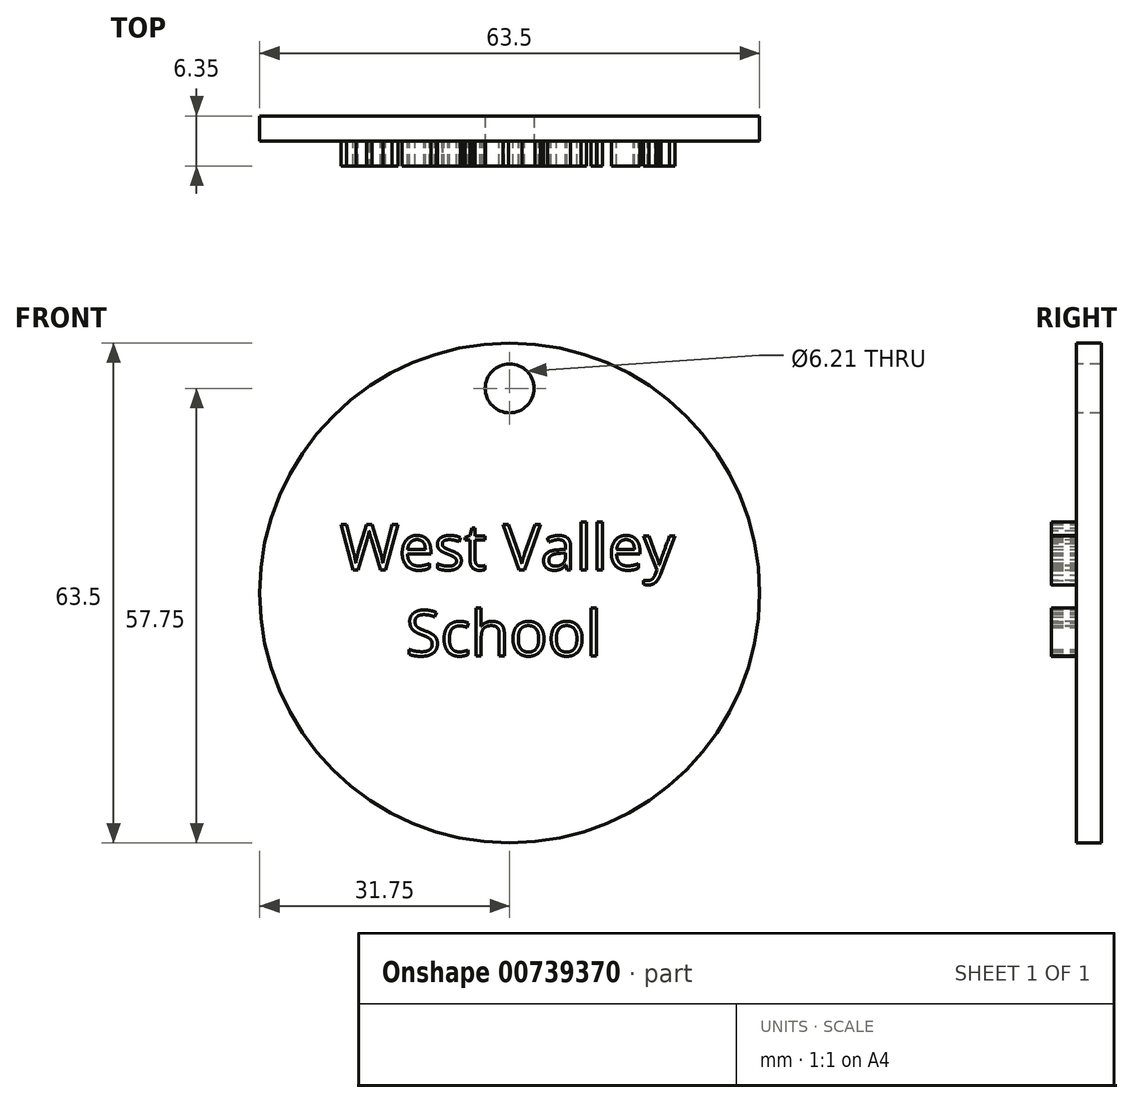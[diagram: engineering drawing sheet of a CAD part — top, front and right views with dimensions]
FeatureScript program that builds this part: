
annotation { "Feature Type Name" : "Feature", "Feature Type Description" : "" }
export const myFeature = defineFeature(function(context is Context, id is Id, definition is map)
    precondition{}
    {
        {
            var Q0;
            Q0=qCreatedBy(makeId("Front.planeOp"),FACE);
            var sketch = newSketch(context, id + "F0", { "sketchPlane" : qUnion([Q0])});
            skCircle(sketch, "E0", {"center": v(0, 0) * mm, "radius": 31.75 * mm});
            skSolve(sketch);
        }
        {
            var Q0;
            Q0=makeQuery(id+"F0.imprint","IMPRINT",FACE,{"disambiguationData":[TD([[makeQuery(id+"F0.imprint","IMPRINT",EDGE,{"derivedFrom":sQuery(id+"F0.wireOp",EDGE,"E0")}),1.0]])]});
            extrude(context, id + "F1", {"entities" : qUnion([Q0]), "depth" : 3.17 * mm, "offsetDistance" : 25.4 * mm});
        }
        {
            var Q0;
            Q0=makeQuery(id+"F1.opExtrude","CAP_FACE",FACE,{"disambiguationData":[OSD([sQuery(id+"F0.wireOp",EDGE,"E0")])],"isStart":false});
            var sketch = newSketch(context, id + "F2", { "sketchPlane" : qUnion([Q0])});
            skText(sketch, "E1", { "text": "West Valley\n    School", "fontName": "OpenSans-Regular.ttf"});
            const initialGuessF2  = {"E1": [-0.02153, 0.00295, 1, 0, 0.00578]};
            skSetInitialGuess(sketch, initialGuessF2);
            skSolve(sketch);
        }
        {
            var Q0;
            Q0 = qSketchRegion(id + "F2", true);
            extrude(context, id + "F3", {"entities" : qUnion([Q0]), "operationType" : NewBodyOperationType.ADD, "depth" : 3.17 * mm, "offsetDistance" : 25.4 * mm});
        }
        {
            var Q0;
            {var subQ0=sQuery(id+"F0.wireOp",EDGE,"E0");Q0=makeQuery(id+"F3.boolean.opBoolean","SPLIT",FACE,{"disambiguationData":[TD([makeQuery(id+"F1.opExtrude","SWEPT_FACE",FACE,{"disambiguationData":[OSD([subQ0])]})])],"derivedFrom":makeQuery(id+"F1.opExtrude","CAP_FACE",FACE,{"disambiguationData":[OSD([subQ0])],"isStart":false})});}
            var sketch = newSketch(context, id + "F4", { "sketchPlane" : qUnion([Q0])});
            skCircle(sketch, "E2", {"center": v(0, 26) * mm, "radius": 3.1 * mm});
            skSolve(sketch);
        }
        {
            var Q0;
            Q0 = qSketchRegion(id + "F4", true);
            extrude(context, id + "F5", {"entities" : qUnion([Q0]), "operationType" : NewBodyOperationType.REMOVE, "endBound" : BoundingType.SYMMETRIC, "oppositeDirection" : true, "depth" : 25.4 * mm, "offsetDistance" : 25.4 * mm});
        }
    });
